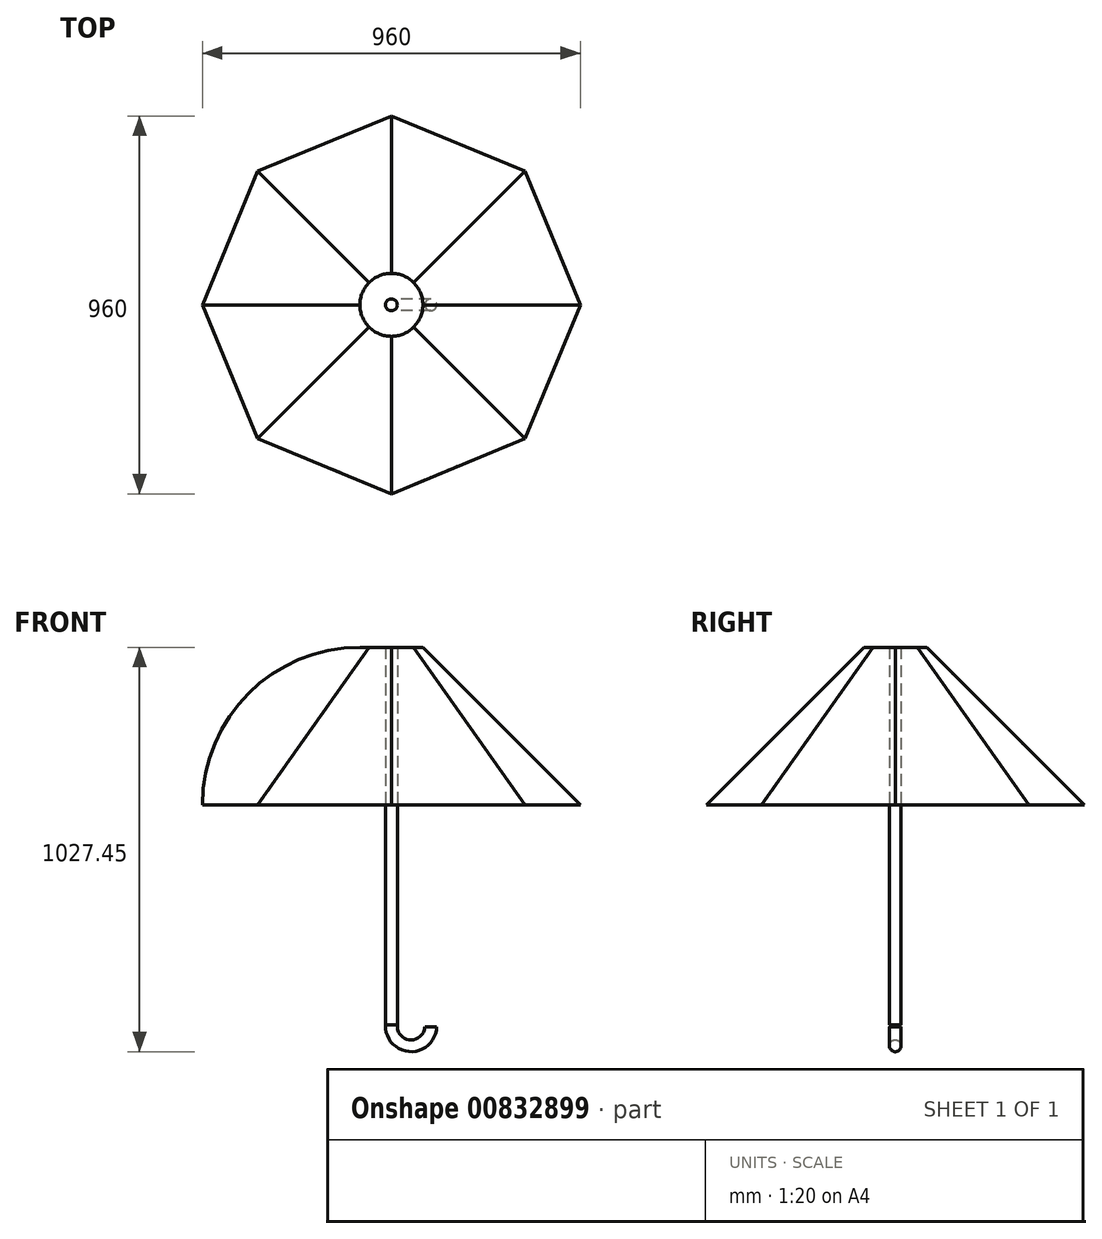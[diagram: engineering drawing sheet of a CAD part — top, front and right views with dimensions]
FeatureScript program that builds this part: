
annotation { "Feature Type Name" : "Feature", "Feature Type Description" : "" }
export const myFeature = defineFeature(function(context is Context, id is Id, definition is map)
    precondition{}
    {
        {
            var Q0;
            Q0=qCreatedBy(makeId("Top.planeOp"),FACE);
            cPlane(context, id + "F0", {"entities" : qUnion([Q0]), "cplaneType" : CPlaneType.OFFSET, "offset" : 400 * mm, "width" : 150 * mm, "height" : 150 * mm});
        }
        {
            var Q0;
            Q0=qCreatedBy(id+"F0.planeOp",FACE);
            var sketch = newSketch(context, id + "F1", { "sketchPlane" : qUnion([Q0])});
            skCircle(sketch, "E0", {"center": v(0, 0) * mm, "radius": 80 * mm});
            skSolve(sketch);
        }
        {
            var Q0;
            Q0=qCreatedBy(makeId("Top.planeOp"),FACE);
            var sketch = newSketch(context, id + "F2", { "sketchPlane" : qUnion([Q0])});
            skCircle(sketch, "E1.cCircle", {"center": v(0, 0) * mm, "radius": 443.46 * mm, "construction": true});
            skLineSegment(sketch, "E1.0", {"start": v(339.41, 339.41) * mm, "end": v(480, 0) * mm});
            skLineSegment(sketch, "E1.1", {"start": v(480, 0) * mm, "end": v(339.41, -339.41) * mm});
            skLineSegment(sketch, "E1.2", {"start": v(339.41, -339.41) * mm, "end": v(0, -480) * mm});
            skLineSegment(sketch, "E1.3", {"start": v(0, -480) * mm, "end": v(-339.41, -339.41) * mm});
            skLineSegment(sketch, "E1.4", {"start": v(-339.41, -339.41) * mm, "end": v(-480, 0) * mm});
            skLineSegment(sketch, "E1.5", {"start": v(-480, 0) * mm, "end": v(-339.41, 339.41) * mm});
            skLineSegment(sketch, "E1.6", {"start": v(-339.41, 339.41) * mm, "end": v(0, 480) * mm});
            skLineSegment(sketch, "E1.7", {"start": v(0, 480) * mm, "end": v(339.41, 339.41) * mm});
            skPoint(sketch, "E1.0.midPoint", {"position": v(409.7, 169.7) * mm});
            skSolve(sketch);
        }
        {
            var Q0;
            Q0=qCreatedBy(makeId("Front.planeOp"),FACE);
            var sketch = newSketch(context, id + "F3", { "sketchPlane" : qUnion([Q0])});
            skArc(sketch, "E2", {"start": v(-80, 400) * mm, "mid": v(-362.84, 282.84) * mm, "end": v(-480, 0) * mm});
            skPoint(sketch, "E3.start.orphan", {"position": v(0, 0) * mm});
            skPoint(sketch, "E4.end.orphan", {"position": v(-80, -102.71) * mm});
            skSolve(sketch);
        }
        {
            var Q0;
            Q0=makeQuery(id+"F1.imprint","IMPRINT",FACE,{"disambiguationData":[TD([[makeQuery(id+"F1.imprint","IMPRINT",EDGE,{"derivedFrom":sQuery(id+"F1.wireOp",EDGE,"E0")}),1.0]])]});
            var Q1;
            Q1=makeQuery(id+"F2.imprint","IMPRINT",FACE,{"disambiguationData":[TD([[makeQuery(id+"F2.imprint","IMPRINT",EDGE,{"derivedFrom":sQuery(id+"F2.wireOp",EDGE,"E1.0")}),-1.0]])]});
            var Q2;
            Q2=sQuery(id+"FD0fqwixcjCeT1a_0.1.F3.wireOp",EDGE,"E2");
            var Q3;
            Q3=sQuery(id+"F3.wireOp",EDGE,"E2");
            var Q4;
            Q4=sQuery(id+"FD0fqwixcjCeT1a_0.7.F3.wireOp",EDGE,"E2");
            var Q5;
            Q5=sQuery(id+"FD0fqwixcjCeT1a_0.6.F3.wireOp",EDGE,"E2");
            var Q6;
            Q6=sQuery(id+"FD0fqwixcjCeT1a_0.5.F3.wireOp",EDGE,"E2");
            var Q7;
            Q7=sQuery(id+"FD0fqwixcjCeT1a_0.4.F3.wireOp",EDGE,"E2");
            var Q8;
            Q8=sQuery(id+"FD0fqwixcjCeT1a_0.3.F3.wireOp",EDGE,"E2");
            var Q9;
            Q9=sQuery(id+"FD0fqwixcjCeT1a_0.2.F3.wireOp",EDGE,"E2");
            loft(context, id + "F4", {"addGuides" : true, "sheetProfilesArray" : [{ "sheetProfileEntities" : qUnion([Q0]) }, { "sheetProfileEntities" : qUnion([Q1]) }], "guidesArray" : [{ "guideEntities" : qUnion([Q2]), "guideDerivativeType" : LoftGuideDerivativeType.DEFAULT, "guideDerivativeMagnitude" : 1 }, { "guideEntities" : qUnion([Q3]), "guideDerivativeType" : LoftGuideDerivativeType.DEFAULT, "guideDerivativeMagnitude" : 1 }, { "guideEntities" : qUnion([Q4]), "guideDerivativeType" : LoftGuideDerivativeType.DEFAULT, "guideDerivativeMagnitude" : 1 }, { "guideEntities" : qUnion([Q5]), "guideDerivativeType" : LoftGuideDerivativeType.DEFAULT, "guideDerivativeMagnitude" : 1 }, { "guideEntities" : qUnion([Q6]), "guideDerivativeType" : LoftGuideDerivativeType.DEFAULT, "guideDerivativeMagnitude" : 1 }, { "guideEntities" : qUnion([Q7]), "guideDerivativeType" : LoftGuideDerivativeType.DEFAULT, "guideDerivativeMagnitude" : 1 }, { "guideEntities" : qUnion([Q8]), "guideDerivativeType" : LoftGuideDerivativeType.DEFAULT, "guideDerivativeMagnitude" : 1 }, { "guideEntities" : qUnion([Q9]), "guideDerivativeType" : LoftGuideDerivativeType.DEFAULT, "guideDerivativeMagnitude" : 1 }]});
        }
        {
            var Q0;
            Q0=makeQuery(id+"F4.opLoft","CAP_FACE",FACE,{"disambiguationData":[OSD([makeQuery(id+"F2.imprint","IMPRINT",FACE,{"disambiguationData":[TD([[makeQuery(id+"F2.imprint","IMPRINT",EDGE,{"derivedFrom":sQuery(id+"F2.wireOp",EDGE,"E1.0")}),-1.0]])]})])],"isStart":true});
            shell(context, id + "F5", {"entities" : qUnion([Q0]), "thickness" : 1 * mm});
        }
        {
            var Q0;
            Q0=qCreatedBy(makeId("Front.planeOp"),FACE);
            var sketch = newSketch(context, id + "F6", { "sketchPlane" : qUnion([Q0])});
            skLineSegment(sketch, "E5", {"start": v(0, 397.6) * mm, "end": v(0, -562.4) * mm});
            skArc(sketch, "E6", {"start": v(0, -562.4) * mm, "mid": v(50, -612.4) * mm, "end": v(100, -562.4) * mm});
            skSolve(sketch);
        }
        {
            var Q0;
            Q0=makeQuery(id+"F1.imprint","IMPRINT",FACE,{"disambiguationData":[TD([[makeQuery(id+"F1.imprint","IMPRINT",EDGE,{"derivedFrom":sQuery(id+"F1.wireOp",EDGE,"E0")}),1.0]])]});
            var sketch = newSketch(context, id + "F7", { "sketchPlane" : qUnion([Q0])});
            skCircle(sketch, "E7", {"center": v(0, 0) * mm, "radius": 15 * mm});
            skSolve(sketch);
        }
        {
            var Q0;
            Q0=makeQuery(id+"F7.imprint","IMPRINT",FACE,{"disambiguationData":[TD([[makeQuery(id+"F7.imprint","IMPRINT",EDGE,{"derivedFrom":sQuery(id+"F7.wireOp",EDGE,"E7")}),1.0]])]});
            var Q1;
            Q1=sQuery(id+"F6.wireOp",EDGE,"E5");
            var Q2;
            Q2=sQuery(id+"F6.wireOp",EDGE,"E6");
            sweep(context, id + "F8", {"profiles" : qUnion([Q0]), "path" : qUnion([Q1, Q2])});
        }
    });
